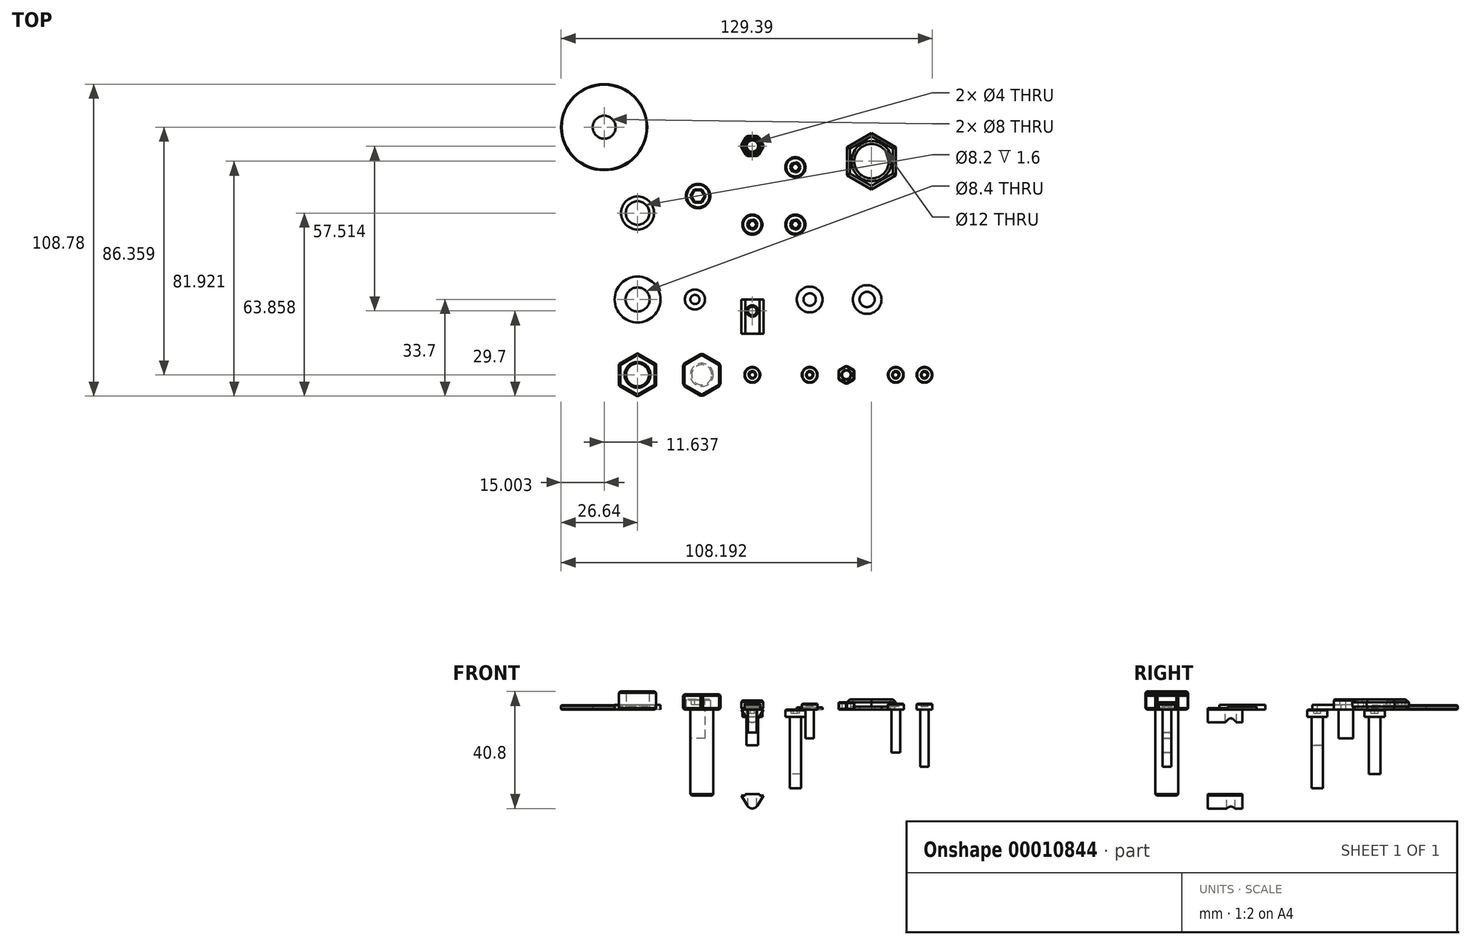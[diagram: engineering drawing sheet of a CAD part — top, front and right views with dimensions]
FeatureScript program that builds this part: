
annotation { "Feature Type Name" : "Feature", "Feature Type Description" : "" }
export const myFeature = defineFeature(function(context is Context, id is Id, definition is map)
    precondition{}
    {
        {
            var Q0;
            Q0=qCreatedBy(makeId("Front.planeOp"),FACE);
            var sketch = newSketch(context, id + "F0", { "sketchPlane" : qUnion([Q0])});
            skLineSegment(sketch, "E0", {"start": v(-3.85, 0) * mm, "end": v(-2.5, 0) * mm});
            skLineSegment(sketch, "E1", {"start": v(-2.5, 0) * mm, "end": v(-2.5, 0.5) * mm});
            skLineSegment(sketch, "E2", {"start": v(-2.5, 0.5) * mm, "end": v(2.5, 0.5) * mm});
            skLineSegment(sketch, "E3", {"start": v(2.5, 0.5) * mm, "end": v(2.5, 0) * mm});
            skLineSegment(sketch, "E4", {"start": v(2.5, 0) * mm, "end": v(3.85, 0) * mm});
            skLineSegment(sketch, "E5", {"start": v(-3.85, 0) * mm, "end": v(-1.71, -3.54) * mm});
            skLineSegment(sketch, "E6", {"start": v(1.71, -3.54) * mm, "end": v(3.85, 0) * mm});
            skPoint(sketch, "E7.visualSharp", {"position": v(0, -6.36) * mm});
            skArc(sketch, "E7.filletArc", {"start": v(-1.71, -3.54) * mm, "mid": v(0, -4.5) * mm, "end": v(1.71, -3.54) * mm});
            skSolve(sketch);
        }
        {
            var Q0;
            Q0=makeQuery(id+"F0.imprint","IMPRINT",FACE,{"disambiguationData":[TD([[makeQuery(id+"F0.imprint","IMPRINT",EDGE,{"derivedFrom":sQuery(id+"F0.wireOp",EDGE,"E0")}),-1.0]])]});
            extrude(context, id + "F1", {"entities" : qUnion([Q0]), "depth" : 12 * mm});
        }
        {
            var Q0;
            Q0=makeQuery(id+"F1.opExtrude","SWEPT_FACE",FACE,{"disambiguationData":[OSD([sQuery(id+"F0.wireOp",EDGE,"E2")])]});
            var sketch = newSketch(context, id + "F2", { "sketchPlane" : qUnion([Q0])});
            skCircle(sketch, "E8", {"center": v(0, -4) * mm, "radius": 2 * mm});
            skSolve(sketch);
        }
        {
            var Q0;
            Q0=makeQuery(id+"F1.opExtrude","SWEPT_BODY",BODY,{"disambiguationData":[OSD([sQuery(id+"F0.wireOp",EDGE,"E0"),sQuery(id+"F0.wireOp",EDGE,"E1"),sQuery(id+"F0.wireOp",EDGE,"E2"),sQuery(id+"F0.wireOp",EDGE,"E3"),sQuery(id+"F0.wireOp",EDGE,"E4"),sQuery(id+"F0.wireOp",EDGE,"E5"),sQuery(id+"F0.wireOp",EDGE,"E6"),sQuery(id+"F0.wireOp",EDGE,"E7.filletArc")])]});
            transform(context, id + "F3", {"entities" : qUnion([Q0]), "transformType" : TransformType.TRANSLATION_3D, "dx" : 0 * mm, "dy" : 0 * mm, "dz" : -30 * mm, "makeCopy" : true});
        }
        {
            var Q0;
            Q0=makeQuery(id+"F2.imprint","IMPRINT",FACE,{"disambiguationData":[TD([[makeQuery(id+"F2.imprint","IMPRINT",EDGE,{"derivedFrom":sQuery(id+"F2.wireOp",EDGE,"E8")}),1.0]])]});
            extrude(context, id + "F4", {"entities" : qUnion([Q0]), "operationType" : NewBodyOperationType.REMOVE, "oppositeDirection" : true, "depth" : 25 * mm});
        }
        {
            var Q0;
            Q0=qCreatedBy(makeId("Top.planeOp"),FACE);
            var sketch = newSketch(context, id + "F5", { "sketchPlane" : qUnion([Q0])});
            skCircle(sketch, "E9", {"center": v(20, 0) * mm, "radius": 2.15 * mm});
            skCircle(sketch, "E10", {"center": v(20, 0) * mm, "radius": 4.5 * mm});
            skCircle(sketch, "E11", {"center": v(40, 0) * mm, "radius": 2.65 * mm});
            skCircle(sketch, "E12", {"center": v(40, 0) * mm, "radius": 5 * mm});
            skCircle(sketch, "E13", {"center": v(-20, 0) * mm, "radius": 1.6 * mm});
            skCircle(sketch, "E14", {"center": v(-20, 0) * mm, "radius": 3.5 * mm});
            skCircle(sketch, "E15", {"center": v(-40, 0) * mm, "radius": 4.2 * mm});
            skCircle(sketch, "E16", {"center": v(-40, 0) * mm, "radius": 8 * mm});
            skCircle(sketch, "E17", {"center": v(0, 26.12) * mm, "radius": 3.5 * mm});
            skCircle(sketch, "E18", {"center": v(0, -26.28) * mm, "radius": 1.5 * mm});
            skCircle(sketch, "E19", {"center": v(0, -26.28) * mm, "radius": 2.75 * mm});
            skCircle(sketch, "E20.cCircle", {"center": v(-40, -26.28) * mm, "radius": 6.5 * mm, "construction": true});
            skLineSegment(sketch, "E20.0", {"start": v(-33.5, -22.52) * mm, "end": v(-33.5, -30.03) * mm});
            skLineSegment(sketch, "E20.1", {"start": v(-33.5, -30.03) * mm, "end": v(-40, -33.78) * mm});
            skLineSegment(sketch, "E20.2", {"start": v(-40, -33.78) * mm, "end": v(-46.5, -30.03) * mm});
            skLineSegment(sketch, "E20.3", {"start": v(-46.5, -30.03) * mm, "end": v(-46.5, -22.52) * mm});
            skLineSegment(sketch, "E20.4", {"start": v(-46.5, -22.52) * mm, "end": v(-40, -18.77) * mm});
            skLineSegment(sketch, "E20.5", {"start": v(-40, -18.77) * mm, "end": v(-33.5, -22.52) * mm});
            skPoint(sketch, "E20.0.midPoint", {"position": v(-33.5, -26.28) * mm});
            skCircle(sketch, "E21", {"center": v(-40, -26.28) * mm, "radius": 4 * mm});
            skCircle(sketch, "E22.cCircle", {"center": v(-17.62, -26.28) * mm, "radius": 6.5 * mm, "construction": true});
            skLineSegment(sketch, "E22.0", {"start": v(-11.12, -22.52) * mm, "end": v(-11.12, -30.03) * mm});
            skLineSegment(sketch, "E22.1", {"start": v(-11.12, -30.03) * mm, "end": v(-17.62, -33.78) * mm});
            skLineSegment(sketch, "E22.2", {"start": v(-17.62, -33.78) * mm, "end": v(-24.12, -30.03) * mm});
            skLineSegment(sketch, "E22.3", {"start": v(-24.12, -30.03) * mm, "end": v(-24.12, -22.52) * mm});
            skLineSegment(sketch, "E22.4", {"start": v(-24.12, -22.52) * mm, "end": v(-17.62, -18.77) * mm});
            skLineSegment(sketch, "E22.5", {"start": v(-17.62, -18.77) * mm, "end": v(-11.12, -22.52) * mm});
            skPoint(sketch, "E22.0.midPoint", {"position": v(-11.12, -26.28) * mm});
            skCircle(sketch, "E23", {"center": v(-17.62, -26.28) * mm, "radius": 4 * mm});
            skCircle(sketch, "E24", {"center": v(-40, 30.16) * mm, "radius": 4.1 * mm});
            skCircle(sketch, "E25", {"center": v(-40, 30.16) * mm, "radius": 5.75 * mm});
            skCircle(sketch, "E26.cCircle", {"center": v(32.77, -26.28) * mm, "radius": 2.75 * mm, "construction": true});
            skLineSegment(sketch, "E26.0", {"start": v(30.02, -24.69) * mm, "end": v(32.77, -23.1) * mm});
            skLineSegment(sketch, "E26.1", {"start": v(32.77, -23.1) * mm, "end": v(35.52, -24.69) * mm});
            skLineSegment(sketch, "E26.2", {"start": v(35.52, -24.69) * mm, "end": v(35.52, -27.86) * mm});
            skLineSegment(sketch, "E26.3", {"start": v(35.52, -27.86) * mm, "end": v(32.77, -29.45) * mm});
            skLineSegment(sketch, "E26.4", {"start": v(32.77, -29.45) * mm, "end": v(30.02, -27.86) * mm});
            skLineSegment(sketch, "E26.5", {"start": v(30.02, -27.86) * mm, "end": v(30.02, -24.69) * mm});
            skPoint(sketch, "E26.0.midPoint", {"position": v(31.4, -23.9) * mm});
            skCircle(sketch, "E27", {"center": v(32.77, -26.28) * mm, "radius": 1.5 * mm});
            skCircle(sketch, "E28", {"center": v(41.55, 48.22) * mm, "radius": 6 * mm});
            skCircle(sketch, "E29.cCircle", {"center": v(41.55, 48.22) * mm, "radius": 8.5 * mm, "construction": true});
            skLineSegment(sketch, "E29.0", {"start": v(50.05, 53.13) * mm, "end": v(50.05, 43.31) * mm});
            skLineSegment(sketch, "E29.1", {"start": v(50.05, 43.31) * mm, "end": v(41.55, 38.4) * mm});
            skLineSegment(sketch, "E29.2", {"start": v(41.55, 38.4) * mm, "end": v(33.05, 43.31) * mm});
            skLineSegment(sketch, "E29.3", {"start": v(33.05, 43.31) * mm, "end": v(33.05, 53.13) * mm});
            skLineSegment(sketch, "E29.4", {"start": v(33.05, 53.13) * mm, "end": v(41.55, 58.04) * mm});
            skLineSegment(sketch, "E29.5", {"start": v(41.55, 58.04) * mm, "end": v(50.05, 53.13) * mm});
            skPoint(sketch, "E29.0.midPoint", {"position": v(50.05, 48.22) * mm});
            skCircle(sketch, "E30.cCircle", {"center": v(0, 53.51) * mm, "radius": 3.5 * mm, "construction": true});
            skLineSegment(sketch, "E30.0", {"start": v(-2.02, 57.01) * mm, "end": v(2.02, 57.01) * mm});
            skLineSegment(sketch, "E30.1", {"start": v(2.02, 57.01) * mm, "end": v(4.04, 53.51) * mm});
            skLineSegment(sketch, "E30.2", {"start": v(4.04, 53.51) * mm, "end": v(2.02, 50.01) * mm});
            skLineSegment(sketch, "E30.3", {"start": v(2.02, 50.01) * mm, "end": v(-2.02, 50.01) * mm});
            skLineSegment(sketch, "E30.4", {"start": v(-2.02, 50.01) * mm, "end": v(-4.04, 53.51) * mm});
            skLineSegment(sketch, "E30.5", {"start": v(-4.04, 53.51) * mm, "end": v(-2.02, 57.01) * mm});
            skPoint(sketch, "E30.0.midPoint", {"position": v(0, 57.01) * mm});
            skCircle(sketch, "E31", {"center": v(0, 53.51) * mm, "radius": 2 * mm});
            skCircle(sketch, "E32", {"center": v(-18.9, 36.09) * mm, "radius": 2.5 * mm});
            skCircle(sketch, "E33", {"center": v(-18.9, 36.09) * mm, "radius": 4.25 * mm});
            skCircle(sketch, "E34", {"center": v(-51.64, 60.08) * mm, "radius": 4 * mm});
            skCircle(sketch, "E35", {"center": v(-51.64, 60.08) * mm, "radius": 15 * mm});
            skSolve(sketch);
        }
        {
            var Q0;
            Q0=makeQuery(id+"F5.imprint","IMPRINT",FACE,{"disambiguationData":[TD([[makeQuery(id+"F5.imprint","IMPRINT",EDGE,{"derivedFrom":sQuery(id+"F5.wireOp",EDGE,"E13")}),-1.0]])]});
            extrude(context, id + "F6", {"entities" : qUnion([Q0]), "depth" : 0.5 * mm});
        }
        {
            var Q0;
            Q0=makeQuery(id+"F5.imprint","IMPRINT",FACE,{"disambiguationData":[TD([[makeQuery(id+"F5.imprint","IMPRINT",EDGE,{"derivedFrom":sQuery(id+"F5.wireOp",EDGE,"E9")}),-1.0]])]});
            extrude(context, id + "F7", {"entities" : qUnion([Q0]), "depth" : 0.8 * mm});
        }
        {
            var Q0;
            Q0=makeQuery(id+"F5.imprint","IMPRINT",FACE,{"disambiguationData":[TD([[makeQuery(id+"F5.imprint","IMPRINT",EDGE,{"derivedFrom":sQuery(id+"F5.wireOp",EDGE,"E11")}),-1.0]])]});
            extrude(context, id + "F8", {"entities" : qUnion([Q0]), "depth" : 1 * mm});
        }
        {
            var Q0;
            Q0=makeQuery(id+"F5.imprint","IMPRINT",FACE,{"disambiguationData":[TD([[makeQuery(id+"F5.imprint","IMPRINT",EDGE,{"derivedFrom":sQuery(id+"F5.wireOp",EDGE,"E15")}),-1.0]])]});
            extrude(context, id + "F9", {"entities" : qUnion([Q0]), "depth" : 1.6 * mm});
        }
        {
            var Q0;
            Q0=makeQuery(id+"F5.imprint","IMPRINT",FACE,{"disambiguationData":[TD([[makeQuery(id+"F5.imprint","IMPRINT",EDGE,{"derivedFrom":sQuery(id+"F5.wireOp",EDGE,"E17")}),1.0]])]});
            extrude(context, id + "F10", {"entities" : qUnion([Q0]), "depth" : 2.5 * mm});
        }
        {
            var Q0;
            Q0=makeQuery(id+"F10.opExtrude","CAP_FACE",FACE,{"disambiguationData":[OSD([sQuery(id+"F5.wireOp",EDGE,"E17")])],"isStart":false});
            var sketch = newSketch(context, id + "F11", { "sketchPlane" : qUnion([Q0])});
            skCircle(sketch, "E36", {"center": v(0, 26.12) * mm, "radius": 2 * mm});
            skSolve(sketch);
        }
        {
            var Q0;
            Q0=makeQuery(id+"F11.imprint","IMPRINT",FACE,{"disambiguationData":[TD([[makeQuery(id+"F11.imprint","IMPRINT",EDGE,{"derivedFrom":sQuery(id+"F11.wireOp",EDGE,"E36")}),1.0]])]});
            extrude(context, id + "F12", {"entities" : qUnion([Q0]), "operationType" : NewBodyOperationType.ADD, "depth" : 10 * mm});
        }
        {
            var Q0;
            Q0=makeQuery(id+"F5.imprint","IMPRINT",FACE,{"disambiguationData":[TD([[makeQuery(id+"F5.imprint","IMPRINT",EDGE,{"derivedFrom":sQuery(id+"F5.wireOp",EDGE,"E17")}),1.0]])]});
            var sketch = newSketch(context, id + "F13", { "sketchPlane" : qUnion([Q0])});
            skCircle(sketch, "E37.cCircle", {"center": v(0, 26.12) * mm, "radius": 1.25 * mm, "construction": true});
            skLineSegment(sketch, "E37.0", {"start": v(-0.72, 27.37) * mm, "end": v(0.72, 27.37) * mm});
            skLineSegment(sketch, "E37.1", {"start": v(0.72, 27.37) * mm, "end": v(1.44, 26.12) * mm});
            skLineSegment(sketch, "E37.2", {"start": v(1.44, 26.12) * mm, "end": v(0.72, 24.87) * mm});
            skLineSegment(sketch, "E37.3", {"start": v(0.72, 24.87) * mm, "end": v(-0.72, 24.87) * mm});
            skLineSegment(sketch, "E37.4", {"start": v(-0.72, 24.87) * mm, "end": v(-1.44, 26.12) * mm});
            skLineSegment(sketch, "E37.5", {"start": v(-1.44, 26.12) * mm, "end": v(-0.72, 27.37) * mm});
            skPoint(sketch, "E37.0.midPoint", {"position": v(0, 27.37) * mm});
            skSolve(sketch);
        }
        {
            var Q0;
            Q0=makeQuery(id+"F13.imprint","IMPRINT",FACE,{"disambiguationData":[TD([[makeQuery(id+"F13.imprint","IMPRINT",EDGE,{"derivedFrom":sQuery(id+"F13.wireOp",EDGE,"E37.0")}),-1.0]])]});
            extrude(context, id + "F14", {"entities" : qUnion([Q0]), "operationType" : NewBodyOperationType.REMOVE, "depth" : 1.25 * mm});
        }
        {
            var Q0;
            Q0=makeQuery(id+"F10.opExtrude","CAP_FACE",FACE,{"disambiguationData":[OSD([sQuery(id+"F5.wireOp",EDGE,"E17")])],"isStart":true});
            chamfer(context, id + "F15", {"entities" : qUnion([Q0]), "width" : 0.3 * mm, "tangentPropagation" : true});
        }
        {
            var Q0;
            Q0=makeQuery(id+"F10.opExtrude","SWEPT_BODY",BODY,{"disambiguationData":[OSD([sQuery(id+"F5.wireOp",EDGE,"E17")])]});
            var Q1;
            Q1=makeQuery(id+"F5.imprint","IMPRINT",FACE,{"disambiguationData":[TD([[makeQuery(id+"F5.imprint","IMPRINT",EDGE,{"derivedFrom":sQuery(id+"F5.wireOp",EDGE,"E17")}),1.0]])]});
            mirror(context, id + "F16", {"entities" : qUnion([Q0]), "mirrorPlane" : qUnion([Q1])});
        }
        {
            var Q0;
            Q0=makeQuery(id+"F10.opExtrude","SWEPT_BODY",BODY,{"disambiguationData":[OSD([sQuery(id+"F5.wireOp",EDGE,"E17")])]});
            deleteBodies(context, id + "F17", {"entities" : qUnion([Q0])});
        }
        {
            var Q0;
            Q0=makeQuery(id+"F16.opPattern","COPY",FACE,{"derivedFrom":makeQuery(id+"F12.opExtrude","CAP_FACE",FACE,{"disambiguationData":[OSD([sQuery(id+"F11.wireOp",EDGE,"E36")])],"isStart":false}),"instanceName":"1"});
            cPlane(context, id + "F18", {"entities" : qUnion([Q0]), "cplaneType" : CPlaneType.OFFSET, "offset" : 2.9 * mm, "oppositeDirection" : true, "width" : 150 * mm, "height" : 150 * mm});
        }
        {
            var Q0;
            Q0=makeQuery(id+"F5.imprint","IMPRINT",FACE,{"disambiguationData":[TD([[makeQuery(id+"F5.imprint","IMPRINT",EDGE,{"derivedFrom":sQuery(id+"F5.wireOp",EDGE,"E18")}),1.0]])]});
            var Q1;
            Q1=makeQuery(id+"F5.imprint","IMPRINT",FACE,{"disambiguationData":[TD([[makeQuery(id+"F5.imprint","IMPRINT",EDGE,{"derivedFrom":sQuery(id+"F5.wireOp",EDGE,"E18")}),-1.0]])]});
            extrude(context, id + "F19", {"entities" : qUnion([Q0, Q1]), "depth" : 2 * mm});
        }
        {
            var Q0;
            Q0=makeQuery(id+"F5.imprint","IMPRINT",FACE,{"disambiguationData":[TD([[makeQuery(id+"F5.imprint","IMPRINT",EDGE,{"derivedFrom":sQuery(id+"F5.wireOp",EDGE,"E18")}),1.0]])]});
            extrude(context, id + "F20", {"entities" : qUnion([Q0]), "operationType" : NewBodyOperationType.ADD, "oppositeDirection" : true, "depth" : 8 * mm});
        }
        {
            var Q0;
            Q0=makeQuery(id+"F19.opExtrude","CAP_FACE",FACE,{"disambiguationData":[OSD([sQuery(id+"F5.wireOp",EDGE,"E19")])],"isStart":false});
            var sketch = newSketch(context, id + "F21", { "sketchPlane" : qUnion([Q0])});
            skCircle(sketch, "E38.cCircle", {"center": v(0, -26.28) * mm, "radius": 1 * mm, "construction": true});
            skLineSegment(sketch, "E38.0", {"start": v(0.58, -27.28) * mm, "end": v(-0.58, -27.28) * mm});
            skLineSegment(sketch, "E38.1", {"start": v(-0.58, -27.28) * mm, "end": v(-1.15, -26.28) * mm});
            skLineSegment(sketch, "E38.2", {"start": v(-1.15, -26.28) * mm, "end": v(-0.58, -25.28) * mm});
            skLineSegment(sketch, "E38.3", {"start": v(-0.58, -25.28) * mm, "end": v(0.58, -25.28) * mm});
            skLineSegment(sketch, "E38.4", {"start": v(0.58, -25.28) * mm, "end": v(1.15, -26.28) * mm});
            skLineSegment(sketch, "E38.5", {"start": v(1.15, -26.28) * mm, "end": v(0.58, -27.28) * mm});
            skPoint(sketch, "E38.0.midPoint", {"position": v(0, -27.28) * mm});
            skSolve(sketch);
        }
        {
            var Q0;
            Q0=makeQuery(id+"F21.imprint","IMPRINT",FACE,{"disambiguationData":[TD([[makeQuery(id+"F21.imprint","IMPRINT",EDGE,{"derivedFrom":sQuery(id+"F21.wireOp",EDGE,"E38.0")}),-1.0]])]});
            extrude(context, id + "F22", {"entities" : qUnion([Q0]), "operationType" : NewBodyOperationType.REMOVE, "oppositeDirection" : true, "depth" : 1 * mm});
        }
        {
            var Q0;
            Q0=makeQuery(id+"F19.opExtrude","CAP_FACE",FACE,{"disambiguationData":[OSD([sQuery(id+"F5.wireOp",EDGE,"E19")])],"isStart":false});
            chamfer(context, id + "F23", {"entities" : qUnion([Q0]), "width" : 0.2 * mm, "tangentPropagation" : true});
        }
        {
            var Q0;
            Q0=makeQuery(id+"F3.opPattern","COPY",FACE,{"derivedFrom":makeQuery(id+"F1.opExtrude","SWEPT_FACE",FACE,{"disambiguationData":[OSD([sQuery(id+"F0.wireOp",EDGE,"E2")])]}),"instanceName":"1"});
            var sketch = newSketch(context, id + "F24", { "sketchPlane" : qUnion([Q0])});
            skCircle(sketch, "E39", {"center": v(0, -4) * mm, "radius": 1.5 * mm});
            skSolve(sketch);
        }
        {
            var Q0;
            Q0=makeQuery(id+"F24.imprint","IMPRINT",FACE,{"disambiguationData":[TD([[makeQuery(id+"F24.imprint","IMPRINT",EDGE,{"derivedFrom":sQuery(id+"F24.wireOp",EDGE,"E39")}),1.0]])]});
            extrude(context, id + "F25", {"entities" : qUnion([Q0]), "operationType" : NewBodyOperationType.REMOVE, "oppositeDirection" : true, "depth" : 25 * mm});
        }
        {
            var Q0;
            Q0=makeQuery(id+"F5.imprint","IMPRINT",FACE,{"disambiguationData":[TD([[makeQuery(id+"F5.imprint","IMPRINT",EDGE,{"derivedFrom":sQuery(id+"F5.wireOp",EDGE,"E20.0")}),-1.0]])]});
            extrude(context, id + "F26", {"entities" : qUnion([Q0]), "depth" : 6.3 * mm});
        }
        {
            var Q0;
            Q0=makeQuery(id+"F26.opExtrude","SWEPT_EDGE",EDGE,{"disambiguationData":[OSD([sQuery(id+"F5.wireOp",EDGE,"E20.1"),sQuery(id+"F5.wireOp",EDGE,"E20.2")])]});
            var Q1;
            Q1=makeQuery(id+"F26.opExtrude","SWEPT_EDGE",EDGE,{"disambiguationData":[OSD([sQuery(id+"F5.wireOp",EDGE,"E20.2"),sQuery(id+"F5.wireOp",EDGE,"E20.3")])]});
            var Q2;
            Q2=makeQuery(id+"F26.opExtrude","SWEPT_EDGE",EDGE,{"disambiguationData":[OSD([sQuery(id+"F5.wireOp",EDGE,"E20.0"),sQuery(id+"F5.wireOp",EDGE,"E20.1")])]});
            var Q3;
            Q3=makeQuery(id+"F26.opExtrude","SWEPT_EDGE",EDGE,{"disambiguationData":[OSD([sQuery(id+"F5.wireOp",EDGE,"E20.3"),sQuery(id+"F5.wireOp",EDGE,"E20.4")])]});
            var Q4;
            Q4=makeQuery(id+"F26.opExtrude","SWEPT_EDGE",EDGE,{"disambiguationData":[OSD([sQuery(id+"F5.wireOp",EDGE,"E20.4"),sQuery(id+"F5.wireOp",EDGE,"E20.5")])]});
            var Q5;
            Q5=makeQuery(id+"F26.opExtrude","SWEPT_EDGE",EDGE,{"disambiguationData":[OSD([sQuery(id+"F5.wireOp",EDGE,"E20.0"),sQuery(id+"F5.wireOp",EDGE,"E20.5")])]});
            fillet(context, id + "F27", {"entities" : qUnion([Q0, Q1, Q2, Q3, Q4, Q5]), "radius" : 0.5 * mm, "tangentPropagation" : true, "allowEdgeOverflow" : false});
        }
        {
            var Q0;
            Q0=makeQuery(id+"F26.opExtrude","CAP_FACE",FACE,{"disambiguationData":[OSD([sQuery(id+"F5.wireOp",EDGE,"E20.0"),sQuery(id+"F5.wireOp",EDGE,"E20.1"),sQuery(id+"F5.wireOp",EDGE,"E20.2"),sQuery(id+"F5.wireOp",EDGE,"E20.3"),sQuery(id+"F5.wireOp",EDGE,"E20.4"),sQuery(id+"F5.wireOp",EDGE,"E20.5"),sQuery(id+"F5.wireOp",EDGE,"E21")])],"isStart":false});
            var Q1;
            Q1=makeQuery(id+"F26.opExtrude","CAP_FACE",FACE,{"disambiguationData":[OSD([sQuery(id+"F5.wireOp",EDGE,"E20.0"),sQuery(id+"F5.wireOp",EDGE,"E20.1"),sQuery(id+"F5.wireOp",EDGE,"E20.2"),sQuery(id+"F5.wireOp",EDGE,"E20.3"),sQuery(id+"F5.wireOp",EDGE,"E20.4"),sQuery(id+"F5.wireOp",EDGE,"E20.5"),sQuery(id+"F5.wireOp",EDGE,"E21")])],"isStart":true});
            chamfer(context, id + "F28", {"entities" : qUnion([Q0, Q1]), "width" : 0.5 * mm, "tangentPropagation" : true});
        }
        {
            var Q0;
            Q0=makeQuery(id+"F5.imprint","IMPRINT",FACE,{"disambiguationData":[TD([[makeQuery(id+"F5.imprint","IMPRINT",EDGE,{"derivedFrom":sQuery(id+"F5.wireOp",EDGE,"E22.0")}),-1.0]])]});
            var Q1;
            Q1=makeQuery(id+"F5.imprint","IMPRINT",FACE,{"disambiguationData":[TD([[makeQuery(id+"F5.imprint","IMPRINT",EDGE,{"derivedFrom":sQuery(id+"F5.wireOp",EDGE,"E23")}),1.0]])]});
            extrude(context, id + "F29", {"entities" : qUnion([Q0, Q1]), "depth" : 5.3 * mm});
        }
        {
            var Q0;
            Q0=makeQuery(id+"F5.imprint","IMPRINT",FACE,{"disambiguationData":[TD([[makeQuery(id+"F5.imprint","IMPRINT",EDGE,{"derivedFrom":sQuery(id+"F5.wireOp",EDGE,"E23")}),1.0]])]});
            extrude(context, id + "F30", {"entities" : qUnion([Q0]), "operationType" : NewBodyOperationType.ADD, "oppositeDirection" : true, "depth" : 30 * mm});
        }
        {
            var Q0;
            Q0=makeQuery(id+"F30.opExtrude","CAP_FACE",FACE,{"disambiguationData":[OSD([sQuery(id+"F5.wireOp",EDGE,"E23")])],"isStart":false});
            var Q1;
            Q1=makeQuery(id+"F29.opExtrude","CAP_FACE",FACE,{"disambiguationData":[OSD([sQuery(id+"F5.wireOp",EDGE,"E22.0"),sQuery(id+"F5.wireOp",EDGE,"E22.1"),sQuery(id+"F5.wireOp",EDGE,"E22.2"),sQuery(id+"F5.wireOp",EDGE,"E22.3"),sQuery(id+"F5.wireOp",EDGE,"E22.4"),sQuery(id+"F5.wireOp",EDGE,"E22.5")])],"isStart":false});
            var Q2;
            Q2=makeQuery(id+"F29.opExtrude","SWEPT_FACE",FACE,{"disambiguationData":[OSD([sQuery(id+"F5.wireOp",EDGE,"E22.1")])]});
            var Q3;
            Q3=makeQuery(id+"F29.opExtrude","SWEPT_FACE",FACE,{"disambiguationData":[OSD([sQuery(id+"F5.wireOp",EDGE,"E22.2")])]});
            var Q4;
            Q4=makeQuery(id+"F29.opExtrude","CAP_EDGE",EDGE,{"disambiguationData":[OSD([sQuery(id+"F5.wireOp",EDGE,"E22.0")])],"isStart":true});
            var Q5;
            Q5=makeQuery(id+"F29.opExtrude","SWEPT_FACE",FACE,{"disambiguationData":[OSD([sQuery(id+"F5.wireOp",EDGE,"E22.5")])]});
            var Q6;
            Q6=makeQuery(id+"F29.opExtrude","SWEPT_FACE",FACE,{"disambiguationData":[OSD([sQuery(id+"F5.wireOp",EDGE,"E22.4")])]});
            var Q7;
            Q7=makeQuery(id+"F29.opExtrude","SWEPT_FACE",FACE,{"disambiguationData":[OSD([sQuery(id+"F5.wireOp",EDGE,"E22.3")])]});
            chamfer(context, id + "F31", {"entities" : qUnion([Q0, Q1, Q2, Q3, Q4, Q5, Q6, Q7]), "width" : 0.5 * mm, "tangentPropagation" : true});
        }
        {
            var Q0;
            Q0=makeQuery(id+"F5.imprint","IMPRINT",FACE,{"disambiguationData":[TD([[makeQuery(id+"F5.imprint","IMPRINT",EDGE,{"derivedFrom":sQuery(id+"F5.wireOp",EDGE,"E24")}),-1.0]])]});
            extrude(context, id + "F32", {"entities" : qUnion([Q0]), "depth" : 1.6 * mm});
        }
        {
            var Q0;
            Q0=makeQuery(id+"F19.opExtrude","SWEPT_BODY",BODY,{"disambiguationData":[OSD([sQuery(id+"F5.wireOp",EDGE,"E19")])]});
            transform(context, id + "F33", {"entities" : qUnion([Q0]), "transformType" : TransformType.TRANSLATION_3D, "dx" : 20 * mm, "dy" : 0 * mm, "dz" : 0 * mm, "makeCopy" : true});
        }
        {
            var Q0;
            Q0=makeQuery(id+"F33.opPattern","COPY",FACE,{"derivedFrom":makeQuery(id+"F20.opExtrude","CAP_FACE",FACE,{"disambiguationData":[OSD([sQuery(id+"F5.wireOp",EDGE,"E18")])],"isStart":false}),"instanceName":"1"});
            extrude(context, id + "F34", {"entities" : qUnion([Q0]), "operationType" : NewBodyOperationType.ADD, "depth" : 2 * mm});
        }
        {
            var Q0;
            Q0=makeQuery(id+"F5.imprint","IMPRINT",FACE,{"disambiguationData":[TD([[makeQuery(id+"F5.imprint","IMPRINT",EDGE,{"derivedFrom":sQuery(id+"F5.wireOp",EDGE,"E26.0")}),-1.0]])]});
            extrude(context, id + "F35", {"entities" : qUnion([Q0]), "depth" : 2.5 * mm});
        }
        {
            var Q0;
            Q0=makeQuery(id+"F35.opExtrude","CAP_FACE",FACE,{"disambiguationData":[OSD([sQuery(id+"F5.wireOp",EDGE,"E26.0"),sQuery(id+"F5.wireOp",EDGE,"E26.1"),sQuery(id+"F5.wireOp",EDGE,"E26.2"),sQuery(id+"F5.wireOp",EDGE,"E26.3"),sQuery(id+"F5.wireOp",EDGE,"E26.4"),sQuery(id+"F5.wireOp",EDGE,"E26.5"),sQuery(id+"F5.wireOp",EDGE,"E27")])],"isStart":false});
            var Q1;
            Q1=makeQuery(id+"F35.opExtrude","CAP_FACE",FACE,{"disambiguationData":[OSD([sQuery(id+"F5.wireOp",EDGE,"E26.0"),sQuery(id+"F5.wireOp",EDGE,"E26.1"),sQuery(id+"F5.wireOp",EDGE,"E26.2"),sQuery(id+"F5.wireOp",EDGE,"E26.3"),sQuery(id+"F5.wireOp",EDGE,"E26.4"),sQuery(id+"F5.wireOp",EDGE,"E26.5"),sQuery(id+"F5.wireOp",EDGE,"E27")])],"isStart":true});
            var Q2;
            Q2=makeQuery(id+"F35.opExtrude","SWEPT_EDGE",EDGE,{"disambiguationData":[OSD([sQuery(id+"F5.wireOp",EDGE,"E26.3"),sQuery(id+"F5.wireOp",EDGE,"E26.4")])]});
            var Q3;
            Q3=makeQuery(id+"F35.opExtrude","SWEPT_EDGE",EDGE,{"disambiguationData":[OSD([sQuery(id+"F5.wireOp",EDGE,"E26.4"),sQuery(id+"F5.wireOp",EDGE,"E26.5")])]});
            var Q4;
            Q4=makeQuery(id+"F35.opExtrude","SWEPT_EDGE",EDGE,{"disambiguationData":[OSD([sQuery(id+"F5.wireOp",EDGE,"E26.2"),sQuery(id+"F5.wireOp",EDGE,"E26.3")])]});
            var Q5;
            Q5=makeQuery(id+"F35.opExtrude","SWEPT_EDGE",EDGE,{"disambiguationData":[OSD([sQuery(id+"F5.wireOp",EDGE,"E26.0"),sQuery(id+"F5.wireOp",EDGE,"E26.5")])]});
            var Q6;
            Q6=makeQuery(id+"F35.opExtrude","SWEPT_EDGE",EDGE,{"disambiguationData":[OSD([sQuery(id+"F5.wireOp",EDGE,"E26.0"),sQuery(id+"F5.wireOp",EDGE,"E26.1")])]});
            var Q7;
            Q7=makeQuery(id+"F35.opExtrude","SWEPT_EDGE",EDGE,{"disambiguationData":[OSD([sQuery(id+"F5.wireOp",EDGE,"E26.1"),sQuery(id+"F5.wireOp",EDGE,"E26.2")])]});
            chamfer(context, id + "F36", {"entities" : qUnion([Q0, Q1, Q2, Q3, Q4, Q5, Q6, Q7]), "width" : 0.2 * mm, "tangentPropagation" : true});
        }
        {
            var Q0;
            Q0=makeQuery(id+"F33.opPattern","COPY",BODY,{"derivedFrom":makeQuery(id+"F19.opExtrude","SWEPT_BODY",BODY,{"disambiguationData":[OSD([sQuery(id+"F5.wireOp",EDGE,"E19")])]}),"instanceName":"1"});
            transform(context, id + "F37", {"entities" : qUnion([Q0]), "transformType" : TransformType.TRANSLATION_3D, "dx" : 30 * mm, "dy" : 0 * mm, "dz" : 0 * mm, "makeCopy" : true});
        }
        {
            var Q0;
            Q0=makeQuery(id+"F37.opPattern","COPY",FACE,{"derivedFrom":makeQuery(id+"F34.opExtrude","CAP_FACE",FACE,{"disambiguationData":[OSD([sQuery(id+"F5.wireOp",EDGE,"E18")])],"isStart":false}),"instanceName":"1"});
            extrude(context, id + "F38", {"entities" : qUnion([Q0]), "operationType" : NewBodyOperationType.ADD, "depth" : 5 * mm});
        }
        {
            var Q0;
            Q0=makeQuery(id+"F37.opPattern","COPY",BODY,{"derivedFrom":makeQuery(id+"F33.opPattern","COPY",BODY,{"derivedFrom":makeQuery(id+"F19.opExtrude","SWEPT_BODY",BODY,{"disambiguationData":[OSD([sQuery(id+"F5.wireOp",EDGE,"E19")])]}),"instanceName":"1"}),"instanceName":"1"});
            transform(context, id + "F39", {"entities" : qUnion([Q0]), "transformType" : TransformType.TRANSLATION_3D, "dx" : 10 * mm, "dy" : 0 * mm, "dz" : 0 * mm, "makeCopy" : true});
        }
        {
            var Q0;
            Q0=makeQuery(id+"F39.opPattern","COPY",FACE,{"derivedFrom":makeQuery(id+"F38.opExtrude","CAP_FACE",FACE,{"disambiguationData":[OSD([sQuery(id+"F5.wireOp",EDGE,"E18")])],"isStart":false}),"instanceName":"1"});
            extrude(context, id + "F40", {"entities" : qUnion([Q0]), "operationType" : NewBodyOperationType.ADD, "depth" : 5 * mm});
        }
        {
            var Q0;
            Q0=makeQuery(id+"F5.imprint","IMPRINT",FACE,{"disambiguationData":[TD([[makeQuery(id+"F5.imprint","IMPRINT",EDGE,{"derivedFrom":sQuery(id+"F5.wireOp",EDGE,"E28")}),-1.0]])]});
            extrude(context, id + "F41", {"entities" : qUnion([Q0]), "depth" : 3.5 * mm});
        }
        {
            var Q0;
            Q0=makeQuery(id+"F41.opExtrude","CAP_FACE",FACE,{"disambiguationData":[OSD([sQuery(id+"F5.wireOp",EDGE,"E28"),sQuery(id+"F5.wireOp",EDGE,"E29.0"),sQuery(id+"F5.wireOp",EDGE,"E29.1"),sQuery(id+"F5.wireOp",EDGE,"E29.2"),sQuery(id+"F5.wireOp",EDGE,"E29.3"),sQuery(id+"F5.wireOp",EDGE,"E29.4"),sQuery(id+"F5.wireOp",EDGE,"E29.5")])],"isStart":false});
            var Q1;
            Q1=makeQuery(id+"F41.opExtrude","CAP_FACE",FACE,{"disambiguationData":[OSD([sQuery(id+"F5.wireOp",EDGE,"E28"),sQuery(id+"F5.wireOp",EDGE,"E29.0"),sQuery(id+"F5.wireOp",EDGE,"E29.1"),sQuery(id+"F5.wireOp",EDGE,"E29.2"),sQuery(id+"F5.wireOp",EDGE,"E29.3"),sQuery(id+"F5.wireOp",EDGE,"E29.4"),sQuery(id+"F5.wireOp",EDGE,"E29.5")])],"isStart":true});
            chamfer(context, id + "F42", {"entities" : qUnion([Q0, Q1]), "width" : 1 * mm, "tangentPropagation" : true});
        }
        {
            var Q0;
            Q0=makeQuery(id+"F16.opPattern","COPY",BODY,{"derivedFrom":makeQuery(id+"F10.opExtrude","SWEPT_BODY",BODY,{"disambiguationData":[OSD([sQuery(id+"F5.wireOp",EDGE,"E17")])]}),"instanceName":"1"});
            transform(context, id + "F43", {"entities" : qUnion([Q0]), "transformType" : TransformType.TRANSLATION_3D, "dx" : 15 * mm, "dy" : 0 * mm, "dz" : 0 * mm, "makeCopy" : true});
        }
        {
            var Q0;
            Q0=makeQuery(id+"F43.opPattern","COPY",FACE,{"derivedFrom":makeQuery(id+"F16.opPattern","COPY",FACE,{"derivedFrom":makeQuery(id+"F12.opExtrude","CAP_FACE",FACE,{"disambiguationData":[OSD([sQuery(id+"F11.wireOp",EDGE,"E36")])],"isStart":false}),"instanceName":"1"}),"instanceName":"1"});
            extrude(context, id + "F44", {"entities" : qUnion([Q0]), "operationType" : NewBodyOperationType.ADD, "depth" : 15 * mm});
        }
        {
            var Q0;
            Q0=makeQuery(id+"F5.imprint","IMPRINT",FACE,{"disambiguationData":[TD([[makeQuery(id+"F5.imprint","IMPRINT",EDGE,{"derivedFrom":sQuery(id+"F5.wireOp",EDGE,"E30.0")}),-1.0]])]});
            extrude(context, id + "F45", {"entities" : qUnion([Q0]), "depth" : 3.2 * mm});
        }
        {
            var Q0;
            Q0=makeQuery(id+"F45.opExtrude","CAP_FACE",FACE,{"disambiguationData":[OSD([sQuery(id+"F5.wireOp",EDGE,"E30.0"),sQuery(id+"F5.wireOp",EDGE,"E30.1"),sQuery(id+"F5.wireOp",EDGE,"E30.2"),sQuery(id+"F5.wireOp",EDGE,"E30.3"),sQuery(id+"F5.wireOp",EDGE,"E30.4"),sQuery(id+"F5.wireOp",EDGE,"E30.5"),sQuery(id+"F5.wireOp",EDGE,"E31")])],"isStart":true});
            var Q1;
            Q1=makeQuery(id+"F45.opExtrude","SWEPT_EDGE",EDGE,{"disambiguationData":[OSD([sQuery(id+"F5.wireOp",EDGE,"E30.3"),sQuery(id+"F5.wireOp",EDGE,"E30.4")])]});
            var Q2;
            Q2=makeQuery(id+"F45.opExtrude","SWEPT_EDGE",EDGE,{"disambiguationData":[OSD([sQuery(id+"F5.wireOp",EDGE,"E30.4"),sQuery(id+"F5.wireOp",EDGE,"E30.5")])]});
            var Q3;
            Q3=makeQuery(id+"F45.opExtrude","SWEPT_EDGE",EDGE,{"disambiguationData":[OSD([sQuery(id+"F5.wireOp",EDGE,"E30.0"),sQuery(id+"F5.wireOp",EDGE,"E30.5")])]});
            var Q4;
            Q4=makeQuery(id+"F45.opExtrude","SWEPT_EDGE",EDGE,{"disambiguationData":[OSD([sQuery(id+"F5.wireOp",EDGE,"E30.2"),sQuery(id+"F5.wireOp",EDGE,"E30.3")])]});
            var Q5;
            Q5=makeQuery(id+"F45.opExtrude","SWEPT_EDGE",EDGE,{"disambiguationData":[OSD([sQuery(id+"F5.wireOp",EDGE,"E30.0"),sQuery(id+"F5.wireOp",EDGE,"E30.1")])]});
            var Q6;
            Q6=makeQuery(id+"F45.opExtrude","SWEPT_EDGE",EDGE,{"disambiguationData":[OSD([sQuery(id+"F5.wireOp",EDGE,"E30.1"),sQuery(id+"F5.wireOp",EDGE,"E30.2")])]});
            var Q7;
            Q7=makeQuery(id+"F45.opExtrude","CAP_FACE",FACE,{"disambiguationData":[OSD([sQuery(id+"F5.wireOp",EDGE,"E30.0"),sQuery(id+"F5.wireOp",EDGE,"E30.1"),sQuery(id+"F5.wireOp",EDGE,"E30.2"),sQuery(id+"F5.wireOp",EDGE,"E30.3"),sQuery(id+"F5.wireOp",EDGE,"E30.4"),sQuery(id+"F5.wireOp",EDGE,"E30.5"),sQuery(id+"F5.wireOp",EDGE,"E31")])],"isStart":false});
            chamfer(context, id + "F46", {"entities" : qUnion([Q0, Q1, Q2, Q3, Q4, Q5, Q6, Q7]), "width" : 0.5 * mm, "tangentPropagation" : true});
        }
        {
            var Q0;
            Q0=makeQuery(id+"F5.imprint","IMPRINT",FACE,{"disambiguationData":[TD([[makeQuery(id+"F5.imprint","IMPRINT",EDGE,{"derivedFrom":sQuery(id+"F5.wireOp",EDGE,"E32")}),1.0]])]});
            extrude(context, id + "F47", {"entities" : qUnion([Q0]), "oppositeDirection" : true, "depth" : 10 * mm});
        }
        {
            var Q0;
            Q0=makeQuery(id+"F5.imprint","IMPRINT",FACE,{"disambiguationData":[TD([[makeQuery(id+"F5.imprint","IMPRINT",EDGE,{"derivedFrom":sQuery(id+"F5.wireOp",EDGE,"E32")}),-1.0]])]});
            var Q1;
            Q1=makeQuery(id+"F5.imprint","IMPRINT",FACE,{"disambiguationData":[TD([[makeQuery(id+"F5.imprint","IMPRINT",EDGE,{"derivedFrom":sQuery(id+"F5.wireOp",EDGE,"E32")}),1.0]])]});
            extrude(context, id + "F48", {"entities" : qUnion([Q0, Q1]), "operationType" : NewBodyOperationType.ADD, "depth" : 3.5 * mm});
        }
        {
            var Q0;
            Q0=makeQuery(id+"F48.opExtrude","CAP_FACE",FACE,{"disambiguationData":[OSD([sQuery(id+"F5.wireOp",EDGE,"E33")])],"isStart":false});
            var sketch = newSketch(context, id + "F49", { "sketchPlane" : qUnion([Q0])});
            skCircle(sketch, "E40.cCircle", {"center": v(-18.9, 36.09) * mm, "radius": 2 * mm, "construction": true});
            skLineSegment(sketch, "E40.0", {"start": v(-20.06, 38.09) * mm, "end": v(-17.75, 38.09) * mm});
            skLineSegment(sketch, "E40.1", {"start": v(-17.75, 38.09) * mm, "end": v(-16.6, 36.09) * mm});
            skLineSegment(sketch, "E40.2", {"start": v(-16.6, 36.09) * mm, "end": v(-17.75, 34.09) * mm});
            skLineSegment(sketch, "E40.3", {"start": v(-17.75, 34.09) * mm, "end": v(-20.06, 34.09) * mm});
            skLineSegment(sketch, "E40.4", {"start": v(-20.06, 34.09) * mm, "end": v(-21.21, 36.09) * mm});
            skLineSegment(sketch, "E40.5", {"start": v(-21.21, 36.09) * mm, "end": v(-20.06, 38.09) * mm});
            skPoint(sketch, "E40.0.midPoint", {"position": v(-18.9, 38.09) * mm});
            skSolve(sketch);
        }
        {
            var Q0;
            Q0=makeQuery(id+"F49.imprint","IMPRINT",FACE,{"disambiguationData":[TD([[makeQuery(id+"F49.imprint","IMPRINT",EDGE,{"derivedFrom":sQuery(id+"F49.wireOp",EDGE,"E40.0")}),-1.0]])]});
            extrude(context, id + "F50", {"entities" : qUnion([Q0]), "operationType" : NewBodyOperationType.REMOVE, "oppositeDirection" : true, "depth" : 1.7 * mm});
        }
        {
            var Q0;
            Q0=makeQuery(id+"F48.opExtrude","CAP_FACE",FACE,{"disambiguationData":[OSD([sQuery(id+"F5.wireOp",EDGE,"E33")])],"isStart":false});
            chamfer(context, id + "F51", {"entities" : qUnion([Q0]), "width" : 0.3 * mm, "tangentPropagation" : true});
        }
        {
            var Q0;
            Q0=makeQuery(id+"F5.imprint","IMPRINT",FACE,{"disambiguationData":[TD([[makeQuery(id+"F5.imprint","IMPRINT",EDGE,{"derivedFrom":sQuery(id+"F5.wireOp",EDGE,"E34")}),-1.0]])]});
            extrude(context, id + "F52", {"entities" : qUnion([Q0]), "depth" : 1.5 * mm});
        }
        {
            var Q0;
            Q0=makeQuery(id+"F52.opExtrude","CAP_EDGE",EDGE,{"disambiguationData":[OSD([sQuery(id+"F5.wireOp",EDGE,"E35")])],"isStart":false});
            var Q1;
            Q1=makeQuery(id+"F52.opExtrude","CAP_EDGE",EDGE,{"disambiguationData":[OSD([sQuery(id+"F5.wireOp",EDGE,"E35")])],"isStart":true});
            chamfer(context, id + "F53", {"entities" : qUnion([Q0, Q1]), "width" : 0.2 * mm, "tangentPropagation" : true});
        }
        {
            var Q0;
            Q0=makeQuery(id+"F43.opPattern","COPY",BODY,{"derivedFrom":makeQuery(id+"F16.opPattern","COPY",BODY,{"derivedFrom":makeQuery(id+"F10.opExtrude","SWEPT_BODY",BODY,{"disambiguationData":[OSD([sQuery(id+"F5.wireOp",EDGE,"E17")])]}),"instanceName":"1"}),"instanceName":"1"});
            transform(context, id + "F54", {"entities" : qUnion([Q0]), "transformType" : TransformType.TRANSLATION_3D, "dx" : 0 * mm, "dy" : 20 * mm, "dz" : 0 * mm, "makeCopy" : true});
        }
        {
            var Q0;
            Q0=makeQuery(id+"F54.opPattern","COPY",FACE,{"derivedFrom":makeQuery(id+"F44.opExtrude","CAP_FACE",FACE,{"disambiguationData":[OSD([sQuery(id+"F11.wireOp",EDGE,"E36")])],"isStart":false}),"instanceName":"1"});
            extrude(context, id + "F55", {"entities" : qUnion([Q0]), "operationType" : NewBodyOperationType.REMOVE, "oppositeDirection" : true, "depth" : 5 * mm});
        }
    });
